# Revit family: ГРЕЕРС Д2
name_source: partatom
category: Wyposażenie mechaniczne
revit_build: Autodesk Revit 2016 (Build: 20150220_1215(x64)
units: mm (PartAtom-declared; Revit-internal decimal feet)

## family parameters
Obiekt nadrzędny = Powierzchnia
Punkt obliczania pomieszczeń = Nie
Tnij formami wycięć po wczytaniu = Nie
Typ części = Normalny
Współdzielony = Nie
Wymiar okrągłego złącza = Użyj średnicy

## types (3) — shared parameters
IP = 54
Model = ГРЕЕРС Д2
Opis = Дестратификатор воздуха
Opis indeksowy = Дестратификатор LEO Д2 производительностью до 5400 м3/ч
Producent = ГРЕЕРС
Sterowanie = Включи/Выключи
URL = www.greers.ru
Вентилятор = Осевой, однофазный, переменного тока с 3-скоростным вентилятором
Вес аппарата = 13.90 kg
Данные продукта = https://greers.ru
Индекс = 22101
Классификация нагрузки = ДВИГАТЕЛЬ
Коэффициент мощности = 1
Макс. потребление тока = 1 A
Материал = ГРЕЕРС-EPP-черный
Напряжение питания = 230 V
Расстояние от перекрытия = 1000 mm  [stored 3.28084 ft]
Стандартное оснащение = brak
zero-valued in all types: Domyślna rzędna

## per-type parameters (varying)
| type | Полная мощность | Производительность |
| ГРЕЕРС Д2, 1 скорость | 230 VA | 3100.0 m³/h |
| ГРЕЕРС Д2, 2 скорость | 276 VA | 4500.0 m³/h |
| ГРЕЕРС Д2, 3 скорость | 322 VA | 5400.0 m³/h |

note: [stored X ft] marks values corroborated as IEEE doubles in the binary element streams (Revit-internal decimal feet)
